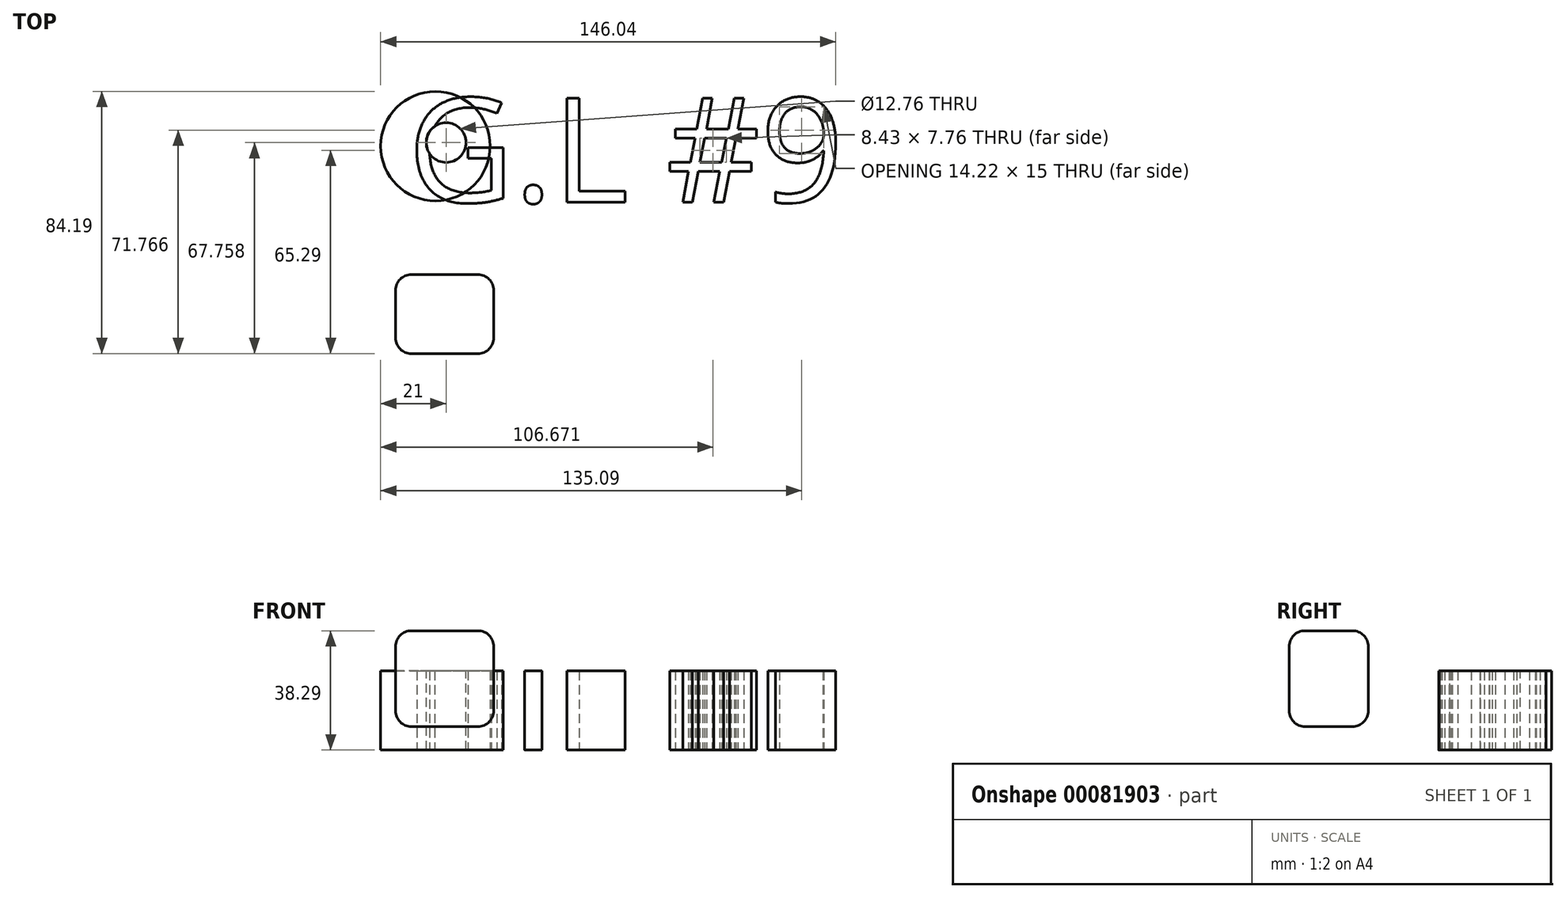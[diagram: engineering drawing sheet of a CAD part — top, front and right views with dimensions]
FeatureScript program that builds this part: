
annotation { "Feature Type Name" : "Feature", "Feature Type Description" : "" }
export const myFeature = defineFeature(function(context is Context, id is Id, definition is map)
    precondition{}
    {
        {
            var Q0;
            Q0=qCreatedBy(makeId("Top.planeOp"),FACE);
            var sketch = newSketch(context, id + "F0", { "sketchPlane" : qUnion([Q0])});
            skText(sketch, "E0", { "text": "G.L #9", "fontName": "OpenSans-Regular.ttf"});
            const initialGuessF0  = {"E0": [-0.0542, 0.02325, 1, 0, 0.03366]};
            skSetInitialGuess(sketch, initialGuessF0);
            skSolve(sketch);
        }
        {
            var Q0;
            Q0 = qSketchRegion(id + "F0", true);
            extrude(context, id + "F1", {"entities" : qUnion([Q0]), "depth" : 25.4 * mm});
        }
        {
            var Q0;
            Q0=qCreatedBy(makeId("Front.planeOp"),FACE);
            var sketch = newSketch(context, id + "F2", { "sketchPlane" : qUnion([Q0])});
            skLineSegment(sketch, "E1.bottom", {"start": v(-58.17, 38.3) * mm, "end": v(-26.64, 38.3) * mm});
            skLineSegment(sketch, "E1.top", {"start": v(-58.17, 7.54) * mm, "end": v(-26.64, 7.54) * mm});
            skLineSegment(sketch, "E1.left", {"start": v(-58.17, 38.3) * mm, "end": v(-58.17, 7.54) * mm});
            skLineSegment(sketch, "E1.right", {"start": v(-26.64, 38.3) * mm, "end": v(-26.64, 7.54) * mm});
            skSolve(sketch);
        }
        {
            var Q0;
            Q0=qCreatedBy(makeId("Top.planeOp"),FACE);
            var sketch = newSketch(context, id + "F3", { "sketchPlane" : qUnion([Q0])});
            skCircle(sketch, "E2", {"center": v(-45.35, 41.22) * mm, "radius": 17.57 * mm});
            skSolve(sketch);
        }
        {
            var Q0;
            Q0=makeQuery(id+"F3.imprint","IMPRINT",FACE,{"disambiguationData":[TD([[makeQuery(id+"F3.imprint","IMPRINT",EDGE,{"derivedFrom":sQuery(id+"F3.wireOp",EDGE,"E2")}),1.0]])]});
            extrude(context, id + "F4", {"entities" : qUnion([Q0]), "depth" : 25.4 * mm});
        }
        {
            var Q0;
            Q0=makeQuery(id+"F2.imprint","IMPRINT",FACE,{"disambiguationData":[TD([[makeQuery(id+"F2.imprint","IMPRINT",EDGE,{"derivedFrom":sQuery(id+"F2.wireOp",EDGE,"E1.bottom")}),-1.0]])]});
            extrude(context, id + "F5", {"entities" : qUnion([Q0]), "depth" : 25.4 * mm});
        }
        {
            var Q0;
            Q0=makeQuery(id+"F5.opExtrude","SWEPT_FACE",FACE,{"disambiguationData":[OSD([sQuery(id+"F2.wireOp",EDGE,"E1.top")])]});
            fillet(context, id + "F6", {"entities" : qUnion([Q0]), "radius" : 5.08 * mm, "tangentPropagation" : true, "allowEdgeOverflow" : false});
        }
        {
            var Q0;
            Q0=makeQuery(id+"F4.opExtrude","CAP_FACE",FACE,{"disambiguationData":[OSD([sQuery(id+"F3.wireOp",EDGE,"E2")])],"isStart":false});
            var sketch = newSketch(context, id + "F7", { "sketchPlane" : qUnion([Q0])});
            skCircle(sketch, "E3", {"center": v(-41.93, 42.36) * mm, "radius": 6.38 * mm});
            skSolve(sketch);
        }
        {
            var Q0;
            Q0=makeQuery(id+"F7.imprint","IMPRINT",FACE,{"disambiguationData":[TD([[makeQuery(id+"F7.imprint","IMPRINT",EDGE,{"derivedFrom":sQuery(id+"F7.wireOp",EDGE,"E3")}),1.0]])]});
            extrude(context, id + "F8", {"entities" : qUnion([Q0]), "operationType" : NewBodyOperationType.REMOVE, "oppositeDirection" : true, "depth" : 25.4 * mm});
        }
        {
            var Q0;
            Q0=qCreatedBy(makeId("Top.planeOp"),FACE);
            var sketch = newSketch(context, id + "F9", { "sketchPlane" : qUnion([Q0])});
            skCircle(sketch, "E4", {"center": v(0, 0) * mm, "radius": 20.54 * mm});
            skSolve(sketch);
        }
        {
            var Q0;
            Q0=qCreatedBy(makeId("Front.planeOp"),FACE);
            var sketch = newSketch(context, id + "F10", { "sketchPlane" : qUnion([Q0])});
            skFitSpline(sketch, "E5", {"points": [v(0, 0) * mm, v(7.99, 10.41) * mm, v(11.98, 13.83) * mm, v(15.4, 18.4) * mm, v(20.82, 22.68) * mm, v(23.96, 28.67) * mm], "startDerivative": vector(31.26, 45.53) * mm, "endDerivative": vector(12.53, 34.09) * mm});
            skSolve(sketch);
        }
        {
            var Q0;
            Q0=makeQuery(id+"F5.opExtrude","SWEPT_FACE",FACE,{"disambiguationData":[OSD([sQuery(id+"F2.wireOp",EDGE,"E1.bottom")])]});
            fillet(context, id + "F11", {"entities" : qUnion([Q0]), "radius" : 5.08 * mm, "tangentPropagation" : true, "allowEdgeOverflow" : false});
        }
        {
            var Q0;
            Q0=makeQuery(id+"F5.opExtrude","SWEPT_FACE",FACE,{"disambiguationData":[OSD([sQuery(id+"F2.wireOp",EDGE,"E1.left")])]});
            fillet(context, id + "F12", {"entities" : qUnion([Q0]), "radius" : 5.08 * mm, "tangentPropagation" : true, "allowEdgeOverflow" : false});
        }
        {
            var Q0;
            Q0=makeQuery(id+"F5.opExtrude","CAP_FACE",FACE,{"disambiguationData":[OSD([sQuery(id+"F2.wireOp",EDGE,"E1.bottom"),sQuery(id+"F2.wireOp",EDGE,"E1.top"),sQuery(id+"F2.wireOp",EDGE,"E1.left"),sQuery(id+"F2.wireOp",EDGE,"E1.right")])],"isStart":false});
            fillet(context, id + "F13", {"entities" : qUnion([Q0]), "radius" : 5.08 * mm, "tangentPropagation" : true, "allowEdgeOverflow" : false});
        }
        {
            var Q0;
            Q0=makeQuery(id+"F5.opExtrude","SWEPT_FACE",FACE,{"disambiguationData":[OSD([sQuery(id+"F2.wireOp",EDGE,"E1.right")])]});
            fillet(context, id + "F14", {"entities" : qUnion([Q0]), "radius" : 5.08 * mm, "tangentPropagation" : true, "allowEdgeOverflow" : false});
        }
    });
